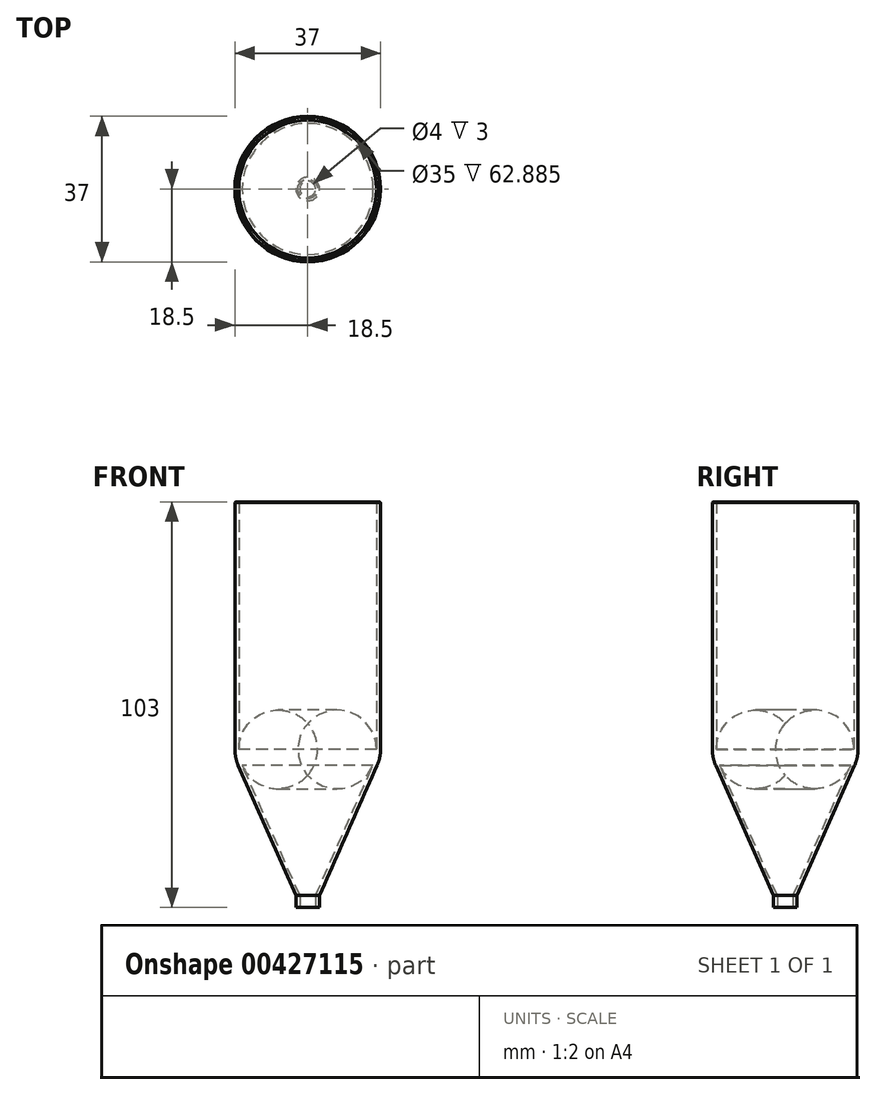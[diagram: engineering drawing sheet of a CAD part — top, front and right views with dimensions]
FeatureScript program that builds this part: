
annotation { "Feature Type Name" : "Feature", "Feature Type Description" : "" }
export const myFeature = defineFeature(function(context is Context, id is Id, definition is map)
    precondition{}
    {
        {
            var Q0;
            Q0=qCreatedBy(makeId("Top.planeOp"),FACE);
            var sketch = newSketch(context, id + "F0", { "sketchPlane" : qUnion([Q0])});
            skCircle(sketch, "E0", {"center": v(0, 0) * mm, "radius": 2 * mm});
            skCircle(sketch, "E1", {"center": v(0, 0) * mm, "radius": 3 * mm});
            skSolve(sketch);
        }
        {
            var Q0;
            Q0 = qSketchRegion(id + "F0", true);
            extrude(context, id + "F1", {"entities" : qUnion([Q0]), "depth" : 3 * mm});
        }
        {
            var Q0;
            Q0=makeQuery(id+"F1.opExtrude","CAP_FACE",FACE,{"disambiguationData":[OSD([sQuery(id+"F0.wireOp",EDGE,"E0"),sQuery(id+"F0.wireOp",EDGE,"E1")])],"isStart":false});
            var sketch = newSketch(context, id + "F2", { "sketchPlane" : qUnion([Q0])});
            skCircle(sketch, "E2.0", {"center": v(0, 0) * mm, "radius": 3 * mm});
            skCircle(sketch, "E2.1", {"center": v(0, 0) * mm, "radius": 2 * mm});
            skSolve(sketch);
        }
        {
            var Q0;
            Q0=makeQuery(id+"F2.imprint","IMPRINT",FACE,{"disambiguationData":[TD([[makeQuery(id+"F2.imprint","IMPRINT",EDGE,{"derivedFrom":sQuery(id+"F2.wireOp",EDGE,"E2.0")}),1.0]])]});
            var Q1;
            Q1 = qBodyType(qCreatedBy(id + "F7" ,EDGE), BodyType.WIRE);
            cPlane(context, id + "F3", {"entities" : qUnion([Q0, Q1]), "cplaneType" : CPlaneType.OFFSET, "offset" : 35 * mm, "width" : 150 * mm, "height" : 150 * mm});
        }
        {
            var Q0;
            Q0=qCreatedBy(id+"F3.planeOp",FACE);
            var sketch = newSketch(context, id + "F4", { "sketchPlane" : qUnion([Q0])});
            skCircle(sketch, "E3", {"center": v(0, 0) * mm, "radius": 17.5 * mm});
            skCircle(sketch, "E4", {"center": v(0, 0) * mm, "radius": 18.5 * mm});
            skSolve(sketch);
        }
        {
            var Q0;
            Q0=qCreatedBy(makeId("Front.planeOp"),FACE);
            var sketch = newSketch(context, id + "F5", { "sketchPlane" : qUnion([Q0])});
            skLineSegment(sketch, "E5", {"start": v(3, 3) * mm, "end": v(18.5, 38) * mm});
            skLineSegment(sketch, "E6", {"start": v(2, 3) * mm, "end": v(17.5, 38) * mm});
            skLineSegment(sketch, "E7", {"start": v(3, 3) * mm, "end": v(2, 3) * mm});
            skLineSegment(sketch, "E8", {"start": v(17.5, 38) * mm, "end": v(18.5, 38) * mm});
            skLineSegment(sketch, "E9", {"start": v(0, 23.11) * mm, "end": v(0, 3.07) * mm, "construction": true});
            skSolve(sketch);
        }
        {
            var Q0;
            Q0=makeQuery(id+"F5.imprint","IMPRINT",FACE,{"disambiguationData":[TD([[makeQuery(id+"F5.imprint","IMPRINT",EDGE,{"derivedFrom":sQuery(id+"F5.wireOp",EDGE,"E5")}),1.0]])]});
            var Q1;
            Q1=sQuery(id+"F5.wireOp",EDGE,"E9");
            var Q2;
            Q2=sQuery(id+"F5.wireOp",EDGE,"E5");
            var Q3;
            Q3=sQuery(id+"F5.wireOp",EDGE,"E6");
            var Q4;
            Q4=sQuery(id+"F5.wireOp",EDGE,"E7");
            var Q5;
            Q5=sQuery(id+"F5.wireOp",EDGE,"E8");
            var Q6;
            Q6=sQuery(id+"F5.wireOp",EDGE,"E9");
            revolve(context, id + "F6", {"entities" : qUnion([Q0]), "surfaceEntities" : qUnion([Q1, Q2, Q3, Q4, Q5]), "axis" : qUnion([Q6]), "revolveType" : RevolveType.FULL});
        }
        {
            var Q0;
            Q0=makeQuery(id+"F4.imprint","IMPRINT",FACE,{"disambiguationData":[TD([[makeQuery(id+"F4.imprint","IMPRINT",EDGE,{"derivedFrom":sQuery(id+"F4.wireOp",EDGE,"E3")}),-1.0]])]});
            var sketch = newSketch(context, id + "F7", { "sketchPlane" : qUnion([Q0])});
            skCircle(sketch, "E10.0.0", {"center": v(0, 0) * mm, "radius": 18.5 * mm});
            skCircle(sketch, "E11.0", {"center": v(0, 0) * mm, "radius": 17.5 * mm});
            skSolve(sketch);
        }
        {
            var Q0;
            Q0 = qSketchRegion(id + "F7", true);
            extrude(context, id + "F8", {"entities" : qUnion([Q0]), "operationType" : NewBodyOperationType.ADD, "depth" : 55 * mm});
        }
        {
            var Q0;
            Q0=makeQuery(id+"F8.boolean.opBoolean","MERGE",EDGE,{"derivedFrom":[makeQuery(id+"F6.opRevolve","SWEPT_EDGE",EDGE,{"disambiguationData":[OSD([sQuery(id+"F5.wireOp",EDGE,"E5"),sQuery(id+"F5.wireOp",EDGE,"E8")])]}),makeQuery(id+"F8.opExtrude","CAP_EDGE",EDGE,{"disambiguationData":[OSD([sQuery(id+"F7.wireOp",EDGE,"E10.0.0")])],"isStart":true})]});
            var Q1;
            Q1=makeQuery(id+"F8.boolean.opBoolean","MERGE",EDGE,{"derivedFrom":[makeQuery(id+"F6.opRevolve","SWEPT_EDGE",EDGE,{"disambiguationData":[OSD([sQuery(id+"F5.wireOp",EDGE,"E6"),sQuery(id+"F5.wireOp",EDGE,"E8")])]}),makeQuery(id+"F8.opExtrude","CAP_EDGE",EDGE,{"disambiguationData":[OSD([sQuery(id+"F7.wireOp",EDGE,"E11.0")])],"isStart":true})]});
            fillet(context, id + "F9", {"entities" : qUnion([Q0, Q1]), "radius" : 10 * mm, "tangentPropagation" : true, "allowEdgeOverflow" : false});
        }
        {
            var Q0;
            Q0=makeQuery(id+"F8.opExtrude","CAP_FACE",FACE,{"disambiguationData":[OSD([sQuery(id+"F7.wireOp",EDGE,"E10.0.0"),sQuery(id+"F7.wireOp",EDGE,"E11.0")])],"isStart":false});
            var sketch = newSketch(context, id + "F10", { "sketchPlane" : qUnion([Q0])});
            skCircle(sketch, "E12.0", {"center": v(0, 0) * mm, "radius": 17.5 * mm});
            skCircle(sketch, "E13", {"center": v(0, 0) * mm, "radius": 18.5 * mm});
            skSolve(sketch);
        }
        {
            var Q0;
            Q0 = qSketchRegion(id + "F10", true);
            extrude(context, id + "F11", {"entities" : qUnion([Q0]), "operationType" : NewBodyOperationType.ADD, "depth" : 10 * mm});
        }
        {
            var Q0;
            Q0=makeQuery(id+"F11.opExtrude","CAP_EDGE",EDGE,{"disambiguationData":[OSD([sQuery(id+"F10.wireOp",EDGE,"E13")])],"isStart":false});
            chamfer(context, id + "F12", {"entities" : qUnion([Q0]), "width" : 0.2 * mm, "tangentPropagation" : true});
        }
    });
